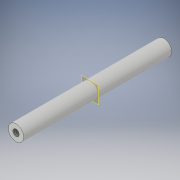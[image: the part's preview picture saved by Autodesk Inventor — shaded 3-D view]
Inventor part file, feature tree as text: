
AUTODESK INVENTOR PART (.ipt)
format: ipt  version: 2017 (Build 210142000, 142)  size: 100,864 bytes
history: native  units: in
note: dims shown in document units (in); Inventor stores cm internally (conversion verified against a paired STEP export)
features: sketch x2, extrude x1, plane x1, hole x1, mirror x1
ambient origin geometry x8: Origin, YZ Plane, XZ Plane, XY Plane, X Axis, Y Axis, Z Axis, Center Point
bodies: Solid1 (feature_tree)
feature tree (6):
  extrude  "Extrusion1"  Depth=3.346in TaperAngle=0.0deg
  plane  "Work Plane1"
  hole  "Hole1"  [1 undecoded]
  mirror  "Mirror1"
  sketch  "Sketch1"  dims[d1=0.35in d2=3.346in d3=0.0in]
  sketch  "Sketch2"  dims[d4=0.0in d5=0.145in d6=0.38in d7=0.375in d8=0.25in d9=0.5635in d10=0.588in d11=0.8108in]
note: 1 required parameter value undecoded (feature->parameter linkage not recoverable at this tier; creation-order binding heuristic only, values carry confidence <= 0.55)
